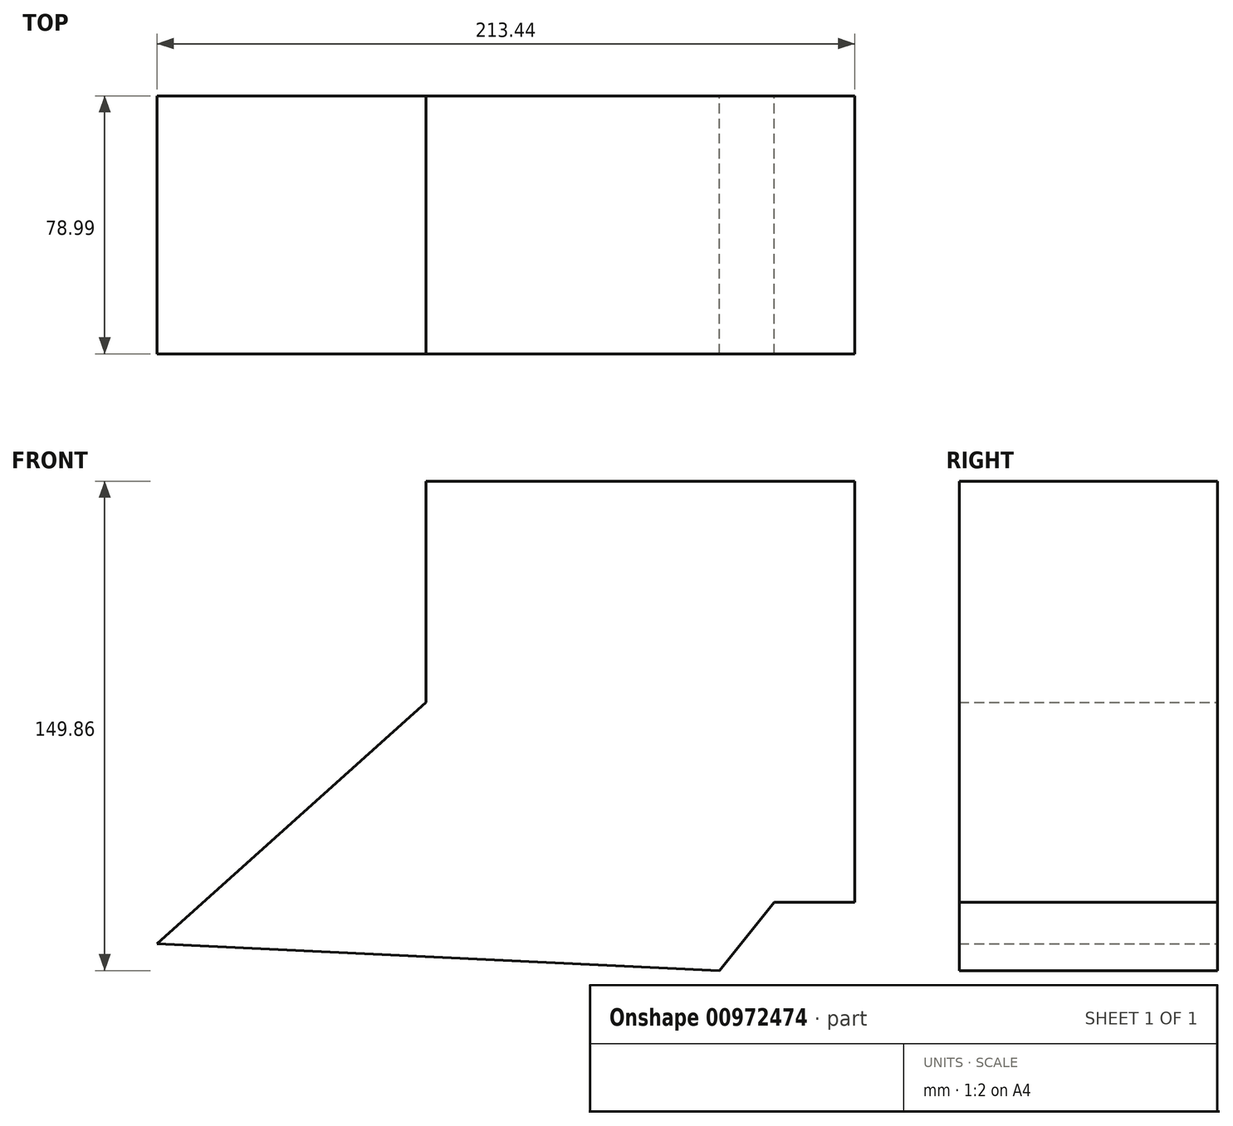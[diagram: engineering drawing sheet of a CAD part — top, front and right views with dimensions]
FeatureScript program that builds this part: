
annotation { "Feature Type Name" : "Feature", "Feature Type Description" : "" }
export const myFeature = defineFeature(function(context is Context, id is Id, definition is map)
    precondition{}
    {
        {
            var Q0;
            Q0=qCreatedBy(makeId("Front.planeOp"),FACE);
            var sketch = newSketch(context, id + "F0", { "sketchPlane" : qUnion([Q0])});
            skLineSegment(sketch, "E0.bottom", {"start": v(0, -21.5) * mm, "end": v(-131.2, -21.5) * mm});
            skLineSegment(sketch, "E0.top", {"start": v(0, 107.43) * mm, "end": v(-131.2, 107.43) * mm});
            skLineSegment(sketch, "E0.left", {"start": v(0, -21.5) * mm, "end": v(0, 107.43) * mm});
            skLineSegment(sketch, "E0.right", {"start": v(-131.2, -21.5) * mm, "end": v(-131.2, 107.43) * mm});
            skPoint(sketch, "E0.middle", {"position": v(-65.6, 42.97) * mm});
            skLineSegment(sketch, "E1", {"start": v(-131.2, 39.72) * mm, "end": v(-213.44, -34.2) * mm});
            skLineSegment(sketch, "E2", {"start": v(-213.44, -34.2) * mm, "end": v(-41.37, -42.43) * mm});
            skLineSegment(sketch, "E3", {"start": v(-41.37, -42.43) * mm, "end": v(0, 9.26) * mm});
            skLineSegment(sketch, "E4", {"start": v(0, 9.26) * mm, "end": v(-131.2, 3.59) * mm});
            skLineSegment(sketch, "E5", {"start": v(-131.2, 3.59) * mm, "end": v(-131.2, 32.45) * mm});
            skLineSegment(sketch, "E6", {"start": v(-131.2, 32.45) * mm, "end": v(-130.9, 39.31) * mm});
            skSolve(sketch);
        }
        {
            var Q0;
            Q0 = qSketchRegion(id + "F0", true);
            extrude(context, id + "F1", {"entities" : qUnion([Q0]), "depth" : 79 * mm, "offsetDistance" : 25.4 * mm});
        }
    });
